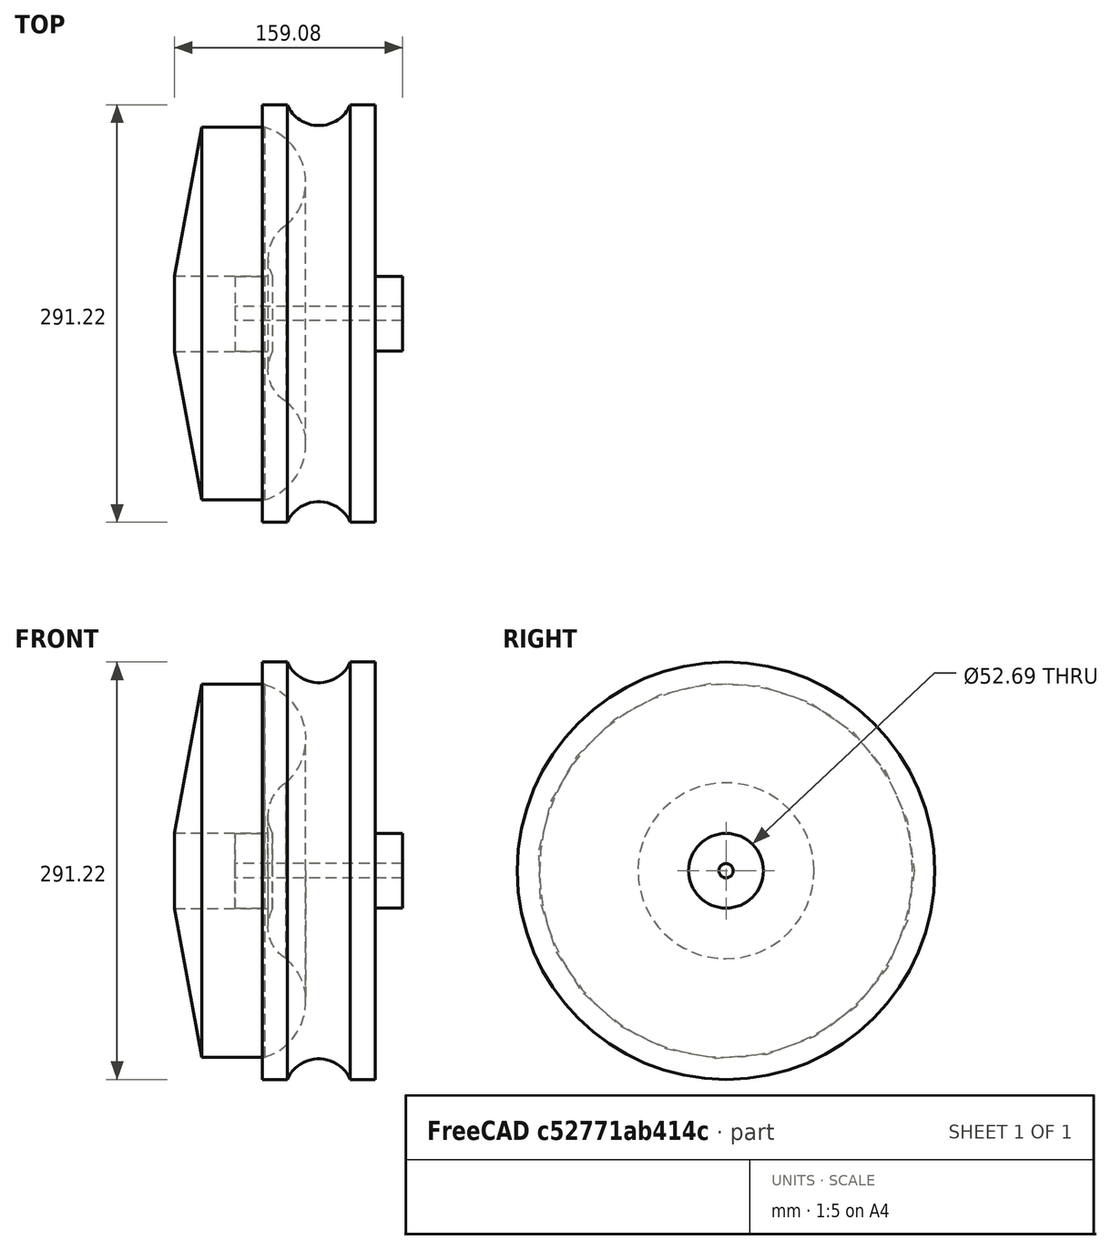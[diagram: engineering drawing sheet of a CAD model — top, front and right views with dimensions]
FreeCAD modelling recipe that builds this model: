
FCSTD DOCUMENT  (FreeCAD 0.16R6705 (Git))
Label: piripicchio
License: All rights reserved
LicenseURL: http://it.wikipedia.org/wiki/<copyright redacted>
objects: Sketcher::SketchObject×3, PartDesign::Revolution×3
note: 9 computed .brp shape members not serialized (recipe doc carries the construction recipe); baked Part::Feature solids carry a one-line shape summary decoded from their .brp

FEATURE [Sketcher::SketchObject] Sketch
  sketch-geometry (10):
    g0: LineSegment StartX=-55.6988 StartY=5 StartZ=0 EndX=-55.6988 EndY=26.0711 EndZ=0
    g1: LineSegment StartX=-55.6988 StartY=26.0711 StartZ=0 EndX=-36.5522 EndY=26.0711 EndZ=0
    g2: LineSegment StartX=-36.5522 StartY=26.0711 StartZ=0 EndX=-36.5522 EndY=145.612 EndZ=0
    g3: LineSegment StartX=-36.5522 StartY=145.612 StartZ=0 EndX=-19.337 EndY=145.612 EndZ=0
    g4: LineSegment StartX=41.971 StartY=145.612 StartZ=0 EndX=41.971 EndY=26.0711 EndZ=0
    g5: LineSegment StartX=41.971 StartY=26.0711 StartZ=0 EndX=61.1176 EndY=26.0711 EndZ=0
    g6: LineSegment StartX=61.1176 StartY=26.0711 StartZ=0 EndX=61.1176 EndY=5 EndZ=0
    g7: LineSegment StartX=61.1176 StartY=5 StartZ=0 EndX=-55.6988 EndY=5 EndZ=0
    g8: ArcOfCircle CenterX=2.7094 CenterY=155.259 CenterZ=0 NormalX=0 NormalY=0 NormalZ=1 Radius=24.0648 StartAngle=3.55408 EndAngle=5.8707
    g9: LineSegment StartX=24.7558 StartY=145.612 StartZ=0 EndX=41.971 EndY=145.612 EndZ=0
  constraints (23):
    c: Coincident(g0,g1)
    c: Coincident(g1,g2)
    c: Coincident(g2,g3)
    c: Coincident(g9,g4)
    c: Coincident(g4,g5)
    c: Coincident(g5,g6)
    c: Coincident(g6,g7)
    c: Coincident(g7,g0)
    c: Vertical(g0)
    c: Horizontal(g7)
    c: Vertical(g6)
    c: Equal(g0,g6)
    c: Horizontal(g1)
    c: Horizontal(g5)
    c: Equal(g5,g1)
    c: Vertical(g2)
    c: Vertical(g4)
    c: Equal(g4,g2)
    c: Coincident(g3,g8)
    c: Coincident(g9,g8)
    c: Tangent(g3,g9)
    c: Equal(g9,g3)
    c: DistanceY(g-1,g6) = 5
FEATURE [PartDesign::Revolution] Revolution  label="ruota"
  Angle = 360
  Axis = (1,0,0)
  Base = (0,0,0)
  ReferenceAxis = -> Sketch [H_Axis]
  Sketch = -> Sketch
FEATURE [Sketcher::SketchObject] Sketch002
  sketch-geometry (5):
    g0: ArcOfCircle CenterX=-46.6114 CenterY=91.585 CenterZ=0 NormalX=0 NormalY=0 NormalZ=1 Radius=40.1531 StartAngle=5.43146 EndAngle=7.56467
    g1: ArcOfCircle CenterX=-6.31154 CenterY=38.8623 CenterZ=0 NormalX=0 NormalY=0 NormalZ=1 Radius=26.4311 StartAngle=2.12241 EndAngle=3.63503
    g2: LineSegment StartX=-35.1561 StartY=130.069 StartZ=0 EndX=-78.7549 EndY=130.069 EndZ=0
    g3: LineSegment StartX=-97.9634 StartY=26.3431 StartZ=0 EndX=-29.5898 EndY=26.3431 EndZ=0
    g4: LineSegment StartX=-78.7549 StartY=130.069 StartZ=0 EndX=-97.9634 EndY=26.3431 EndZ=0
  constraints (7):
    c: Coincident(g1,g0)
    c: Coincident(g1,g3)
    c: Horizontal(g3)
    c: Coincident(g2,g0)
    c: Horizontal(g2)
    c: Coincident(g2,g4)
    c: Coincident(g3,g4)
FEATURE [PartDesign::Revolution] Revolution002  label="dasottrarre"
  Angle = 360
  Axis = (1,0,0)
  Base = (0,0,0)
  ReferenceAxis = -> Sketch002 [H_Axis]
  Sketch = -> Sketch002
FEATURE [Sketcher::SketchObject] Sketch003
  sketch-geometry (5):
    g0: ArcOfCircle CenterX=-46.6114 CenterY=91.585 CenterZ=0 NormalX=0 NormalY=0 NormalZ=1 Radius=40.1531 StartAngle=5.43146 EndAngle=7.56467
    g1: ArcOfCircle CenterX=-6.31154 CenterY=38.8623 CenterZ=0 NormalX=0 NormalY=0 NormalZ=1 Radius=26.4311 StartAngle=2.12241 EndAngle=3.63503
    g2: LineSegment StartX=-35.1561 StartY=130.069 StartZ=0 EndX=-78.7549 EndY=130.069 EndZ=0
    g3: LineSegment StartX=-97.9634 StartY=26.3431 StartZ=0 EndX=-29.5898 EndY=26.3431 EndZ=0
    g4: LineSegment StartX=-78.7549 StartY=130.069 StartZ=0 EndX=-97.9634 EndY=26.3431 EndZ=0
  constraints (7):
    c: Coincident(g1,g0)
    c: Coincident(g1,g3)
    c: Horizontal(g3)
    c: Coincident(g2,g0)
    c: Horizontal(g2)
    c: Coincident(g2,g4)
    c: Coincident(g3,g4)
FEATURE [PartDesign::Revolution] Revolution003  label="dasottrarre001"
  Angle = 360
  Axis = (1,0,0)
  Base = (0,0,0)
  ReferenceAxis = -> Sketch003 [H_Axis]
  Sketch = -> Sketch003
